# Revit family: 06-37-003-DN50-300
name_source: partatom
category: Pipe Accessories
units: mm (PartAtom-declared; Revit-internal decimal feet)

## family parameters
Always vertical = No
Cut with Voids When Loaded = No
Part Type = Valve - Breaks Into
Round Connector Dimension = Use Diameter
Shared = No
Work Plane-Based = No

## types (7) — shared parameters
Body_Wallthickness = 15 mm  [stored 0.0492126 ft]
DN050_PN16 = 06-050-37-09620
DN080_PN16 = 06-080-37-09620
DN100_PN16 = 06-100-37-09620
DN150_PN16 = 06-150-37-09620
DN200_PN16 = 06-200-37-09620
DN250_PN16 = 06-250-37-09620
DN300_PN16 = 06-300-37-09620
Description_ = AVK GATE VALVE, GROOVED ENDS
Ftc = 4 mm  [stored 0.0131234 ft]
Name_Height_reference = 10 mm  [stored 0.0328084 ft]
Rib_Thickness = 18 mm  [stored 0.0590551 ft]
Search_table = 06-37-003-DN50-300
URL product pages = https://www.avkvalves.com
zero-valued in all types: Bottom_Reference

## per-type parameters (varying)
- DN 050: At=40 mm  [stored 0.131234 ft]; Body_Height=100.5 mm; Body_depth=80 mm; Body_width=65 mm; Bonnet_Flange_Depth=118 mm; Bonnet_Flange_Width=82 mm; Bonnet_Flange_cut=7.5 mm  [stored 0.0246063 ft]; Bonnet_Flange_thickness=15 mm  [stored 0.0492126 ft]; Bonnet_Height=41.25 mm  [stored 0.135335 ft]; Bonnet_Reference_height=90.5 mm; Bonnet_Thickness=66.3 mm; Bt=66.3 mm; Bt_2=59 mm; CL _Thickness=21.5 mm  [stored 0.0705381 ft]; CL_Height=45 mm; Cut_Reference=356 mm; D=30 mm  [stored 0.0984252 ft]; D2=127 mm; F1=16 mm  [stored 0.0524934 ft]; Fillet_Thickness=6 mm  [stored 0.019685 ft]; Flange_OR=82.5 mm; Flange_Thickness=19 mm  [stored 0.062336 ft]; Flange_Thickness_cut=28.75 mm; Ftc_reference_height=82.5 mm; H=329 mm; H1=202 mm; H3=367 mm; HW_Dia=15 mm  [stored 0.0492126 ft]; HW_H_ref=7.5 mm  [stored 0.0246063 ft]; HW_Rib_depth=152 mm; HW_Rib_width=15 mm  [stored 0.0492126 ft]; Horizontal_Flange_width=76 mm; ID (Radius)=25 mm  [stored 0.082021 ft]; L=178 mm; L_Dia=50 mm; Name_Reference=71 mm; Name_Width=32.5 mm  [stored 0.106627 ft]; Neck_H=56.5 mm; Neck_T=19.5 mm  [stored 0.0639764 ft]; Neck_T2=17.5 mm  [stored 0.0574147 ft]; Nominal Diameter (DN)=50 mm; R1tv=825 mm; R2f=15 mm  [stored 0.0492126 ft]; RF_Dia=49 mm; Rf=126.67 mm; Rib_Height_Reference_1=120 mm; Rib_Height_Reference_2=110 mm; Rib_Height_Reference_3=100 mm; Rib_Height_Reference_4=60 mm; Rib_Width_1=32.5 mm  [stored 0.106627 ft]; Rib_Width_2=32.5 mm  [stored 0.106627 ft]; Rib_Width_3=32.5 mm  [stored 0.106627 ft]; Rib_depth_1=32.5 mm  [stored 0.106627 ft]; Rib_depth_2=32.5 mm  [stored 0.106627 ft]; Rib_depth_3=32.5 mm  [stored 0.106627 ft]; Rt=275 mm; W=180 mm; W_ref=82.5 mm
- DN 080: At=62.5 mm; Body_Height=136 mm; Body_depth=125 mm; Body_width=75 mm; Bonnet_Flange_Depth=160 mm; Bonnet_Flange_Width=96 mm; Bonnet_Flange_cut=7.5 mm  [stored 0.0246063 ft]; Bonnet_Flange_thickness=15 mm  [stored 0.0492126 ft]; Bonnet_Height=50 mm; Bonnet_Reference_height=126 mm; Bonnet_Thickness=76.5 mm; Bt=76.5 mm; Bt_2=69 mm; CL _Thickness=26.5 mm  [stored 0.0869423 ft]; CL_Height=67.5 mm; Cut_Reference=406 mm; D=44.5 mm; D2=135 mm; F1=20 mm  [stored 0.0656168 ft]; Fillet_Thickness=6 mm  [stored 0.019685 ft]; Flange_OR=100 mm; Flange_Thickness=19 mm  [stored 0.062336 ft]; Flange_Thickness_cut=30 mm  [stored 0.0984252 ft]; Ftc_reference_height=100 mm; H=382 mm; H1=247 mm; H3=435 mm; HW_Dia=15 mm  [stored 0.0492126 ft]; HW_H_ref=7.5 mm  [stored 0.0246063 ft]; HW_Rib_depth=197 mm; HW_Rib_width=15 mm  [stored 0.0492126 ft]; Horizontal_Flange_width=106 mm; ID (Radius)=40 mm  [stored 0.131234 ft]; L=203 mm; L_Dia=80 mm; Name_Reference=90 mm; Name_Width=37.5 mm; Neck_H=43.5 mm; Neck_T=24.5 mm  [stored 0.0803806 ft]; Neck_T2=22.5 mm  [stored 0.0738189 ft]; Nominal Diameter (DN)=80 mm; R1tv=1000 mm; R2f=15 mm  [stored 0.0492126 ft]; RF_Dia=66.9 mm; Rf=176.67 mm; Rib_Height_Reference_1=120 mm; Rib_Height_Reference_2=110 mm; Rib_Height_Reference_3=100 mm; Rib_Height_Reference_4=85 mm; Rib_Width_1=37.5 mm; Rib_Width_2=37.5 mm; Rib_Width_3=37.5 mm; Rib_depth_1=37.5 mm; Rib_depth_2=37.5 mm; Rib_depth_3=37.5 mm; Rt=333.33 mm; W=225 mm; W_ref=105 mm
- DN 100: At=76.5 mm; Body_Height=148 mm; Body_depth=153 mm; Body_width=80 mm; Bonnet_Flange_Depth=180 mm; Bonnet_Flange_Width=81 mm; Bonnet_Flange_cut=7.5 mm  [stored 0.0246063 ft]; Bonnet_Flange_thickness=15 mm  [stored 0.0492126 ft]; Bonnet_Height=55 mm; Bonnet_Reference_height=138 mm; Bonnet_Thickness=81.6 mm; Bt=81.6 mm; Bt_2=74 mm; CL _Thickness=29 mm  [stored 0.0951444 ft]; CL_Height=81.5 mm; Cut_Reference=458 mm; D=57 mm; D2=144 mm; F1=22 mm  [stored 0.0721785 ft]; Fillet_Thickness=6 mm  [stored 0.019685 ft]; Flange_OR=110 mm; Flange_Thickness=19 mm  [stored 0.062336 ft]; Flange_Thickness_cut=30 mm  [stored 0.0984252 ft]; Ftc_reference_height=110 mm; H=414 mm; H1=270 mm; H3=480 mm; HW_Dia=15 mm  [stored 0.0492126 ft]; HW_H_ref=7.5 mm  [stored 0.0246063 ft]; HW_Rib_depth=252 mm; HW_Rib_width=15 mm  [stored 0.0492126 ft]; Horizontal_Flange_width=132 mm; ID (Radius)=50 mm; L=229 mm; L_Dia=100 mm; Name_Reference=101 mm; Name_Width=40 mm  [stored 0.131234 ft]; Neck_H=40.5 mm  [stored 0.132874 ft]; Neck_T=27 mm  [stored 0.0885827 ft]; Neck_T2=25 mm  [stored 0.082021 ft]; Nominal Diameter (DN)=100 mm; R1tv=1100 mm; R2f=15 mm  [stored 0.0492126 ft]; RF_Dia=76.5 mm; Rf=220 mm; Rib_Height_Reference_1=120 mm; Rib_Height_Reference_2=110 mm; Rib_Height_Reference_3=100 mm; Rib_Height_Reference_4=90 mm; Rib_Width_1=40 mm  [stored 0.131234 ft]; Rib_Width_2=40 mm  [stored 0.131234 ft]; Rib_Width_3=40 mm  [stored 0.131234 ft]; Rib_depth_1=40 mm  [stored 0.131234 ft]; Rib_depth_2=40 mm  [stored 0.131234 ft]; Rib_depth_3=40 mm  [stored 0.131234 ft]; Rt=366.67 mm; W=280 mm; W_ref=132.5 mm
- DN 150: At=109 mm; Body_Height=205 mm; Body_depth=218 mm; Body_width=95 mm; Bonnet_Flange_Depth=250 mm; Bonnet_Flange_Width=116 mm; Bonnet_Flange_cut=7.5 mm  [stored 0.0246063 ft]; Bonnet_Flange_thickness=15 mm  [stored 0.0492126 ft]; Bonnet_Height=71.25 mm; Bonnet_Reference_height=195 mm; Bonnet_Thickness=96.9 mm; Bt=96.9 mm; Bt_2=89 mm; CL _Thickness=33.5 mm; CL_Height=114 mm; Cut_Reference=534 mm; D=84 mm; D2=175 mm; F1=22 mm  [stored 0.0721785 ft]; Fillet_Thickness=12 mm  [stored 0.0393701 ft]; Flange_OR=142.5 mm; Flange_Thickness=19 mm  [stored 0.062336 ft]; Flange_Thickness_cut=33.75 mm  [stored 0.110728 ft]; Ftc_reference_height=142.5 mm; H=540 mm; H1=365 mm; H3=649 mm; HW_Dia=15 mm  [stored 0.0492126 ft]; HW_H_ref=7.5 mm  [stored 0.0246063 ft]; HW_Rib_depth=292 mm; HW_Rib_width=15 mm  [stored 0.0492126 ft]; Horizontal_Flange_width=218 mm; ID (Radius)=75 mm; L=267 mm; L_Dia=150 mm; Name_Reference=143 mm; Name_Width=47.5 mm; Neck_H=46 mm; Neck_T=31.5 mm  [stored 0.103346 ft]; Neck_T2=29.5 mm; Nominal Diameter (DN)=150 mm; R1tv=1425 mm; R2f=30 mm  [stored 0.0984252 ft]; RF_Dia=104.5 mm; Rf=363.33 mm; Rib_Height_Reference_1=120 mm; Rib_Height_Reference_2=110 mm; Rib_Height_Reference_3=100 mm; Rib_Height_Reference_4=150 mm; Rib_Width_1=47.5 mm; Rib_Width_2=47.5 mm; Rib_Width_3=47.5 mm; Rib_depth_1=47.5 mm; Rib_depth_2=47.5 mm; Rib_depth_3=47.5 mm; Rt=475 mm; W=320 mm; W_ref=152.5 mm
- DN 200: At=185 mm; Body_Height=250 mm; Body_depth=370 mm; Body_width=120 mm; Bonnet_Flange_Depth=380 mm; Bonnet_Flange_Width=186 mm; Bonnet_Flange_cut=12.5 mm  [stored 0.0410105 ft]; Bonnet_Flange_thickness=25 mm  [stored 0.082021 ft]; Bonnet_Height=85 mm; Bonnet_Reference_height=240 mm; Bonnet_Thickness=122.4 mm; Bt=122.4 mm; Bt_2=114 mm; CL _Thickness=40 mm  [stored 0.131234 ft]; CL_Height=190 mm; Cut_Reference=584 mm; D=109.5 mm; D2=232 mm; F1=28 mm  [stored 0.0918635 ft]; Fillet_Thickness=24 mm  [stored 0.0787402 ft]; Flange_OR=170 mm; Flange_Thickness=20 mm  [stored 0.0656168 ft]; Flange_Thickness_cut=35 mm  [stored 0.114829 ft]; Ftc_reference_height=170 mm; H=688 mm; H1=456 mm; H3=825 mm; HW_Dia=20 mm  [stored 0.0656168 ft]; HW_H_ref=10 mm  [stored 0.0328084 ft]; HW_Rib_depth=322 mm; HW_Rib_width=20 mm  [stored 0.0656168 ft]; Horizontal_Flange_width=274 mm; ID (Radius)=100 mm; L=292 mm; L_Dia=200 mm; Name_Reference=183 mm; Name_Width=60 mm; Neck_H=16 mm  [stored 0.0524934 ft]; Neck_T=38 mm  [stored 0.124672 ft]; Neck_T2=36 mm; Nominal Diameter (DN)=200 mm; R1tv=1700 mm; R2f=60 mm; RF_Dia=132 mm; Rf=456.67 mm; Rib_Height_Reference_1=120 mm; Rib_Height_Reference_2=110 mm; Rib_Height_Reference_3=100 mm; Rib_Height_Reference_4=180 mm; Rib_Width_1=60 mm; Rib_Width_2=60 mm; Rib_Width_3=60 mm; Rib_depth_1=60 mm; Rib_depth_2=60 mm; Rib_depth_3=60 mm; Rt=566.67 mm; W=360 mm; W_ref=170 mm
- DN 250: At=195 mm; Body_Height=305 mm; Body_depth=390 mm; Body_width=124 mm; Bonnet_Flange_Depth=400 mm; Bonnet_Flange_Width=158 mm; Bonnet_Flange_cut=12.5 mm  [stored 0.0410105 ft]; Bonnet_Flange_thickness=25 mm  [stored 0.082021 ft]; Bonnet_Height=100 mm; Bonnet_Reference_height=295 mm; Bonnet_Thickness=126.48 mm; Bt=126.48 mm; Bt_2=118 mm; CL _Thickness=42 mm  [stored 0.137795 ft]; CL_Height=200 mm; Cut_Reference=660 mm; D=136.5 mm; D2=225 mm; F1=27 mm  [stored 0.0885827 ft]; Fillet_Thickness=24 mm  [stored 0.0787402 ft]; Flange_OR=200 mm; Flange_Thickness=22 mm  [stored 0.0721785 ft]; Flange_Thickness_cut=37.5 mm; Ftc_reference_height=200 mm; H=780 mm; H1=555 mm; H3=925 mm; HW_Dia=20 mm  [stored 0.0656168 ft]; HW_H_ref=10 mm  [stored 0.0328084 ft]; HW_Rib_depth=462 mm; HW_Rib_width=20 mm  [stored 0.0656168 ft]; Horizontal_Flange_width=290 mm; ID (Radius)=125 mm; L=330 mm; L_Dia=250 mm; Name_Reference=270 mm; Name_Width=62 mm; Neck_H=50 mm; Neck_T=40 mm  [stored 0.131234 ft]; Neck_T2=38 mm  [stored 0.124672 ft]; Nominal Diameter (DN)=250 mm; R1tv=2000 mm; R2f=60 mm; RF_Dia=159.5 mm; Rf=483.33 mm; Rib_Height_Reference_1=90 mm; Rib_Height_Reference_2=110 mm; Rib_Height_Reference_3=100 mm; Rib_Height_Reference_4=200 mm; Rib_Width_1=180 mm; Rib_Width_2=180 mm; Rib_Width_3=62 mm; Rib_depth_1=400 mm; Rib_depth_2=62 mm; Rib_depth_3=62 mm; Rt=666.67 mm; W=500 mm; W_ref=240 mm
- DN 300: At=208.5 mm; Body_Height=370 mm; Body_depth=417 mm; Body_width=157 mm; Bonnet_Flange_Depth=448 mm; Bonnet_Flange_Width=206 mm; Bonnet_Flange_cut=17.5 mm  [stored 0.0574147 ft]; Bonnet_Flange_thickness=35 mm  [stored 0.114829 ft]; Bonnet_Height=113.75 mm; Bonnet_Reference_height=360 mm; Bonnet_Thickness=160.14 mm; Bt=160.14 mm; Bt_2=151 mm; CL _Thickness=58.5 mm; CL_Height=213.5 mm; Cut_Reference=712 mm; D=162 mm; D2=225 mm; F1=27 mm  [stored 0.0885827 ft]; Fillet_Thickness=24 mm  [stored 0.0787402 ft]; Flange_OR=227.5 mm; Flange_Thickness=24.5 mm  [stored 0.0803806 ft]; Flange_Thickness_cut=38.75 mm  [stored 0.127133 ft]; Ftc_reference_height=227.5 mm; H=855 mm; H1=630 mm; H3=1025 mm; HW_Dia=25 mm  [stored 0.082021 ft]; HW_H_ref=12.5 mm  [stored 0.0410105 ft]; HW_Rib_depth=452 mm; HW_Rib_width=25 mm  [stored 0.082021 ft]; Horizontal_Flange_width=340 mm; ID (Radius)=150 mm; L=356 mm; L_Dia=300 mm; Name_Reference=250 mm; Name_Width=78.5 mm; Neck_H=46.5 mm; Neck_T=56.5 mm; Neck_T2=54.5 mm; Nominal Diameter (DN)=300 mm; R1tv=2275 mm; R2f=60 mm; RF_Dia=183.5 mm; Rf=566.67 mm; Rib_Height_Reference_1=178 mm; Rib_Height_Reference_2=285 mm; Rib_Height_Reference_3=150 mm; Rib_Height_Reference_4=300 mm; Rib_Width_1=195 mm; Rib_Width_2=195 mm; Rib_Width_3=78.5 mm; Rib_depth_1=465 mm; Rib_depth_2=465 mm; Rib_depth_3=78.5 mm; Rt=758.33 mm; W=500 mm; W_ref=237.5 mm

note: [stored X ft] marks values corroborated as IEEE doubles in the binary element streams (Revit-internal decimal feet)

## geometry (parser evidence)
native form markers: Extrusion x1, Sweep x5
no freeform markers — native parametric forms only
